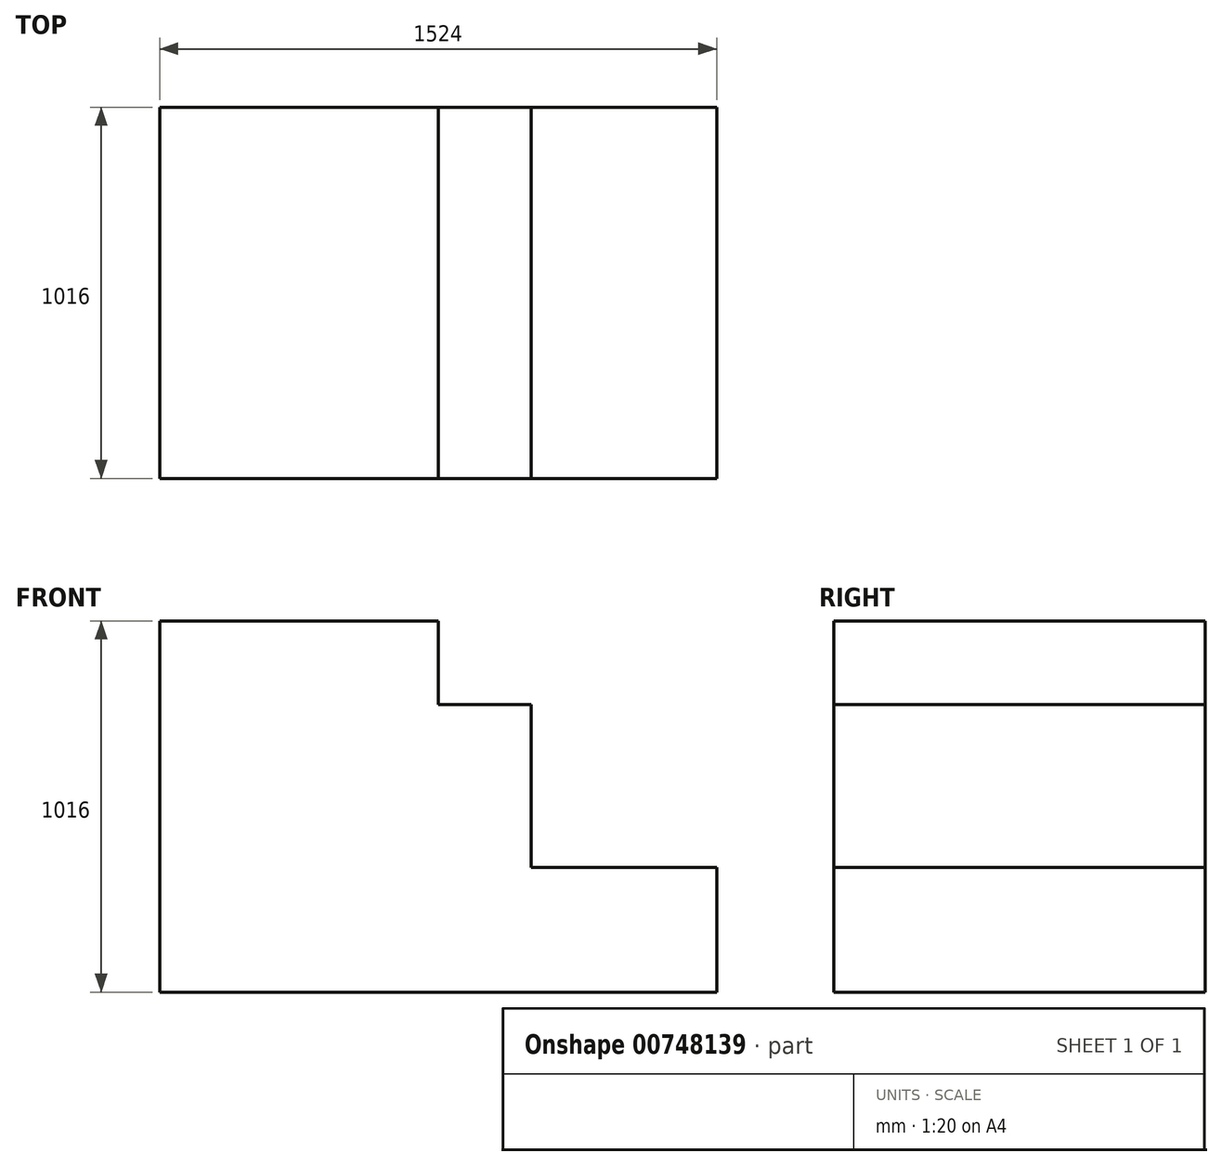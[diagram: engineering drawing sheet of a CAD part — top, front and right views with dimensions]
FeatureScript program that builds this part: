
annotation { "Feature Type Name" : "Feature", "Feature Type Description" : "" }
export const myFeature = defineFeature(function(context is Context, id is Id, definition is map)
    precondition{}
    {
        {
            var Q0;
            Q0=qCreatedBy(makeId("Front.planeOp"),FACE);
            var sketch = newSketch(context, id + "F0", { "sketchPlane" : qUnion([Q0])});
            skLineSegment(sketch, "E0", {"start": v(0, 228.55) * mm, "end": v(0, -787.45) * mm});
            skLineSegment(sketch, "E1", {"start": v(0, -787.45) * mm, "end": v(1524, -787.45) * mm});
            skLineSegment(sketch, "E2", {"start": v(1524, -787.45) * mm, "end": v(1524, -446.12) * mm});
            skLineSegment(sketch, "E3", {"start": v(1524, -446.12) * mm, "end": v(1016, -446.12) * mm});
            skLineSegment(sketch, "E4", {"start": v(1016, -446.12) * mm, "end": v(1016, 0) * mm});
            skLineSegment(sketch, "E5", {"start": v(1016, 0) * mm, "end": v(762, 0) * mm});
            skLineSegment(sketch, "E6", {"start": v(762, 0) * mm, "end": v(762, 228.55) * mm});
            skLineSegment(sketch, "E7", {"start": v(762, 228.55) * mm, "end": v(0, 228.55) * mm});
            skSolve(sketch);
        }
        {
            var Q0;
            Q0 = qSketchRegion(id + "F0", true);
            extrude(context, id + "F1", {"entities" : qUnion([Q0]), "depth" : 1016 * mm, "offsetDistance" : 25.4 * mm});
        }
    });
